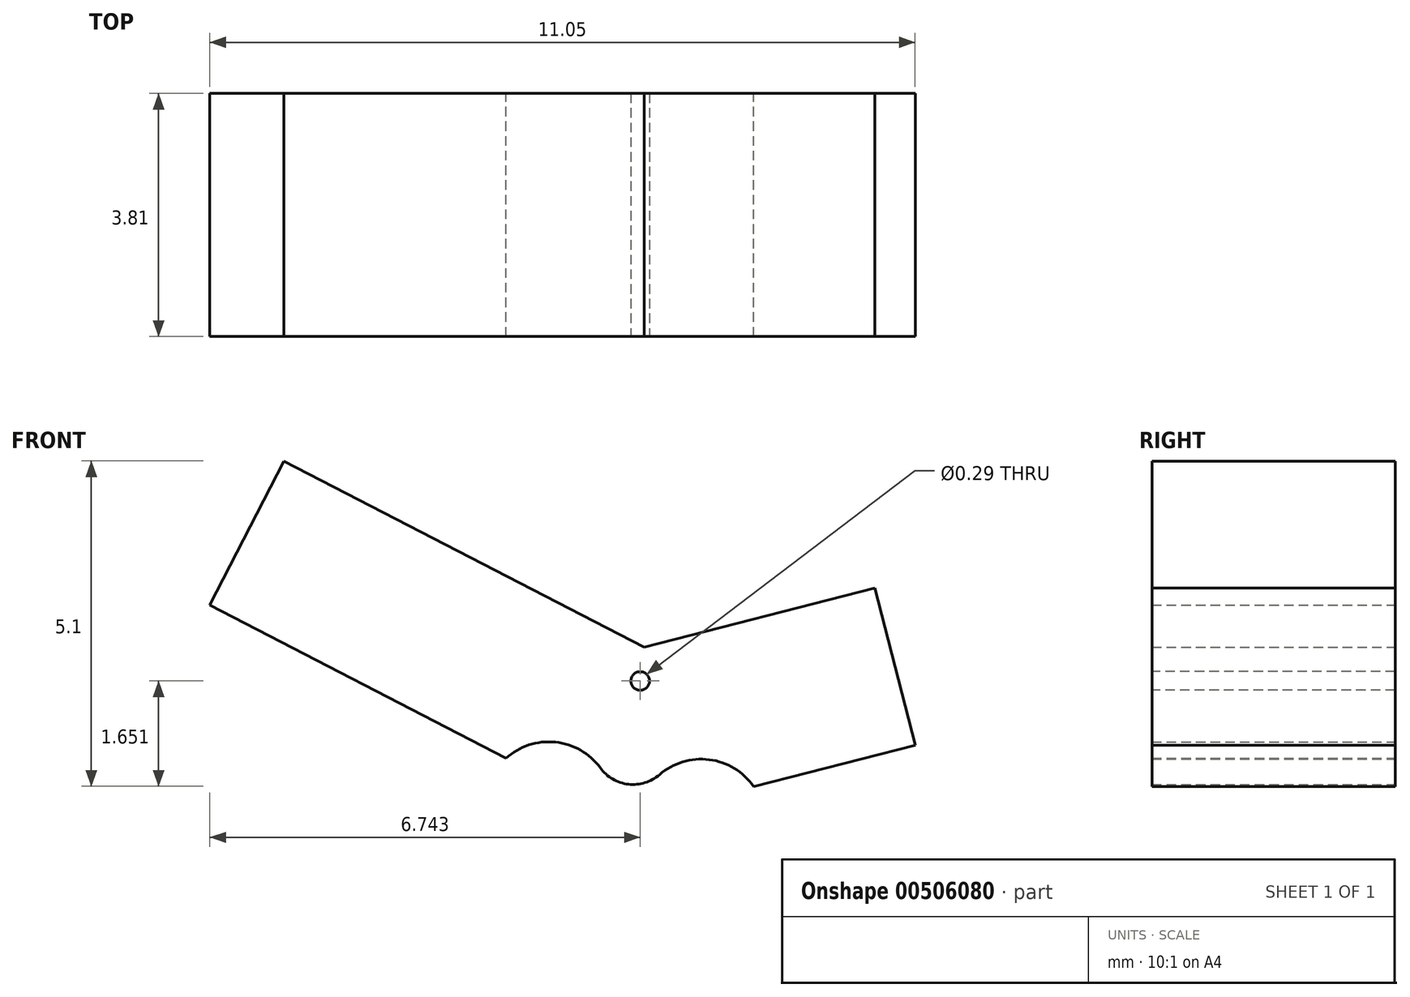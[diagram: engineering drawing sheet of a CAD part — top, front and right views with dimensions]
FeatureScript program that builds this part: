
annotation { "Feature Type Name" : "Feature", "Feature Type Description" : "" }
export const myFeature = defineFeature(function(context is Context, id is Id, definition is map)
    precondition{}
    {
        {
            var Q0;
            Q0=qCreatedBy(makeId("Front.planeOp"),FACE);
            var sketch = newSketch(context, id + "F0", { "sketchPlane" : qUnion([Q0])});
            skLineSegment(sketch, "E0", {"start": v(-0.8, 21.52) * mm, "end": v(4.84, 18.6) * mm});
            skLineSegment(sketch, "E1", {"start": v(4.84, 18.6) * mm, "end": v(11, 20.17) * mm});
            skLineSegment(sketch, "E2", {"start": v(11, 20.17) * mm, "end": v(11.62, 17.71) * mm});
            skLineSegment(sketch, "E3", {"start": v(-1.96, 19.26) * mm, "end": v(-0.8, 21.52) * mm});
            skArc(sketch, "E4", {"start": v(2.68, 16.86) * mm, "mid": v(3.7, 17.05) * mm, "end": v(4.35, 16.23) * mm});
            skArc(sketch, "E5", {"start": v(4.76, 16.06) * mm, "mid": v(5.54, 16.83) * mm, "end": v(6.56, 16.42) * mm});
            skPoint(sketch, "E6.visualSharp", {"position": v(4.6, 16.4) * mm});
            skPoint(sketch, "E7.newPointA", {"position": v(0.77, 17.33) * mm});
            skLineSegment(sketch, "E8", {"start": v(-1.96, 19.26) * mm, "end": v(2.68, 16.86) * mm});
            skLineSegment(sketch, "E9", {"start": v(6.56, 16.42) * mm, "end": v(11.62, 17.71) * mm});
            skArc(sketch, "E10", {"start": v(4.16, 16.7) * mm, "mid": v(4.6, 16.45) * mm, "end": v(5.09, 16.6) * mm});
            skLineSegment(sketch, "E11", {"start": v(1.71, 17.36) * mm, "end": v(2.68, 16.86) * mm, "construction": true});
            skLineSegment(sketch, "E12", {"start": v(4.4, 15.87) * mm, "end": v(6.56, 16.42) * mm, "construction": true});
            skSolve(sketch);
        }
        {
            var Q0;
            Q0 = qSketchRegion(id + "F0", true);
            extrude(context, id + "F1", {"entities" : qUnion([Q0]), "depth" : 3.8 * mm});
        }
        {
            var Q0;
            Q0=makeQuery(id+"F1.opExtrude","CAP_FACE",FACE,{"disambiguationData":[OSD([sQuery(id+"F0.wireOp",EDGE,"E0"),sQuery(id+"F0.wireOp",EDGE,"E1"),sQuery(id+"F0.wireOp",EDGE,"E2"),sQuery(id+"F0.wireOp",EDGE,"E3"),sQuery(id+"F0.wireOp",EDGE,"E4"),sQuery(id+"F0.wireOp",EDGE,"E5"),sQuery(id+"F0.wireOp",EDGE,"E8"),sQuery(id+"F0.wireOp",EDGE,"E9"),sQuery(id+"F0.wireOp",EDGE,"E10")])],"isStart":false});
            var sketch = newSketch(context, id + "F2", { "sketchPlane" : qUnion([Q0])});
            skLineSegment(sketch, "E13", {"start": v(4.84, 18.6) * mm, "end": v(4.6, 16.45) * mm, "construction": true});
            skCircle(sketch, "E14", {"center": v(4.78, 18.07) * mm, "radius": 0.15 * mm});
            skSolve(sketch);
        }
        {
            var Q0;
            Q0=makeQuery(id+"F2.imprint","IMPRINT",FACE,{"disambiguationData":[TD([[makeQuery(id+"F2.imprint","IMPRINT",EDGE,{"derivedFrom":sQuery(id+"F2.wireOp",EDGE,"E14")}),1.0]])]});
            extrude(context, id + "F3", {"entities" : qUnion([Q0]), "operationType" : NewBodyOperationType.REMOVE, "endBound" : BoundingType.UP_TO_NEXT, "oppositeDirection" : true, "depth" : 25.4 * mm});
        }
        {
            var Q0;
            Q0=makeQuery(id+"F1.opExtrude","CAP_FACE",FACE,{"disambiguationData":[OSD([sQuery(id+"F0.wireOp",EDGE,"E0"),sQuery(id+"F0.wireOp",EDGE,"E1"),sQuery(id+"F0.wireOp",EDGE,"E2"),sQuery(id+"F0.wireOp",EDGE,"E3"),sQuery(id+"F0.wireOp",EDGE,"E4"),sQuery(id+"F0.wireOp",EDGE,"E5"),sQuery(id+"F0.wireOp",EDGE,"E8"),sQuery(id+"F0.wireOp",EDGE,"E9"),sQuery(id+"F0.wireOp",EDGE,"E10")])],"isStart":false});
            var sketch = newSketch(context, id + "F4", { "sketchPlane" : qUnion([Q0])});
            skLineSegment(sketch, "E15.bottom", {"start": v(11, 20.17) * mm, "end": v(8.46, 19.53) * mm});
            skLineSegment(sketch, "E15.top", {"start": v(11.62, 17.71) * mm, "end": v(9.1, 17.07) * mm});
            skLineSegment(sketch, "E15.left", {"start": v(11, 20.17) * mm, "end": v(11.62, 17.71) * mm});
            skPoint(sketch, "E16", {"position": v(9.1, 17.07) * mm});
            skLineSegment(sketch, "E17", {"start": v(8.46, 19.53) * mm, "end": v(9.1, 17.07) * mm});
            skSolve(sketch);
        }
        {
            var Q0;
            Q0=makeQuery(id+"F4.imprint","IMPRINT",FACE,{"disambiguationData":[TD([[makeQuery(id+"F4.imprint","IMPRINT",EDGE,{"derivedFrom":sQuery(id+"F4.wireOp",EDGE,"E15.bottom")}),-1.0]])]});
            extrude(context, id + "F5", {"entities" : qUnion([Q0]), "operationType" : NewBodyOperationType.REMOVE, "oppositeDirection" : true, "depth" : 25.4 * mm});
        }
    });
